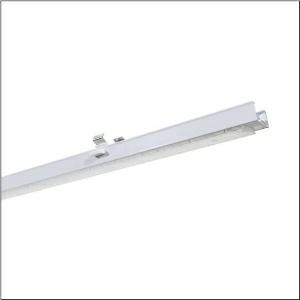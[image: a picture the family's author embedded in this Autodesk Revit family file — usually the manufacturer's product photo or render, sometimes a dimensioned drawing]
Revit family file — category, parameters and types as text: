
# Revit family: trunking_flex_31_51re12mb18b
name_source: partatom
category: Lighting Fixtures
units: mm (PartAtom-declared; Revit-internal decimal feet)

## family parameters
Cut with Voids When Loaded = No
Host = Face
Light Source = No
Part Type = Normal
Room Calculation Point = No
Round Connector Dimension = Use Diameter
Shared = No

## types (1)
- --- (1 x LED, 8000 lm, 50 W, 3500K)
    Apparent Load = 50 VA
    CIE Flux Codes = 65 91 98 99 100
    Color Rendering = 80
    Color Temperature = 3500K
    Default Elevation = 1800 mm
    Description = Trunking Flex 31, luminaire insert, of extruded aluminium section, coated, traffic white (RAL 9016), length: 1.472mm, width: 91mm, height: 53mm, LED rated luminous flux: 8.000lm, light colour: 835, SDCM (Standard Deviation of Colour Matching)MacAdam ≤ 3 SDCM (initial), control gear: ON/OFF Multilumen, with system connector: socket, mains connection: 220..240V, AC, 50/60Hz, rated input power: 50W, luminous flux adjustable on luminaire in four steps (4130/5610/6850/8000lm), connected load according to luminous flux setting (25/34/42/50W), primary light control with lens, of plastic, primary optical cover: cover, of PMMA, light emission: direct distribution, protection rating (complete): IP20, insulation class (complete): insulation class I (protective earthing), certification: CE, UKCA, impact resistance: IK02, permissible ambient temperature for indoor applications: -20..+40°C, packaging unit: 1 piece
    Height = 58 mm
    Lamp = 1 x LED
    Lamp Light Flux = 8000 lm
    Lamp Power = 50 W
    Lamp count = 1
    Length = 1472 mm
    Luminous efficacy = 160 lm/W
    Manufacturer = Siteco
    ModVariant = No
    Model = 51RE12MB18B
    Mounting Place = Ceiling
    Mounting Type = Pendant
    Number of Poles = 1
    OnlyDefault = Yes
    Power Factor = 1
    Product Name = Trunking Flex 31
    Product group = luminaire insert | ceiling pendant
    ProductGroupID = 901
    Protection Class = Protection class I
    Protection Degree = IP 20
    RLX_Detail_Level = 1
    RLX_Emergency_Light_Flux = 0 lm
    RLX_Emergency_Type = 0
    RLX_Emergency_Type_DB = No
    RlxData = <blob elided: 20457 chars, md5=2e1adc8e>
    Socket = socket
    Standby Power = 0 W
    System Light Flux = 8000 lm
    System Power = 50 W
    Type Comments = factory setting: luminous flux: 100 % | (ON | ON) | 300 mA
    Type Image = l_1266702.jpg
    URL = http://relux.com
    VarID = @adj_065553
    Voltage = 0 V
    Weight = 0.00 kg
    Width = 65 mm

## geometry (parser evidence)
native form markers: Blend x4, Sweep x11
no freeform markers — native parametric forms only
